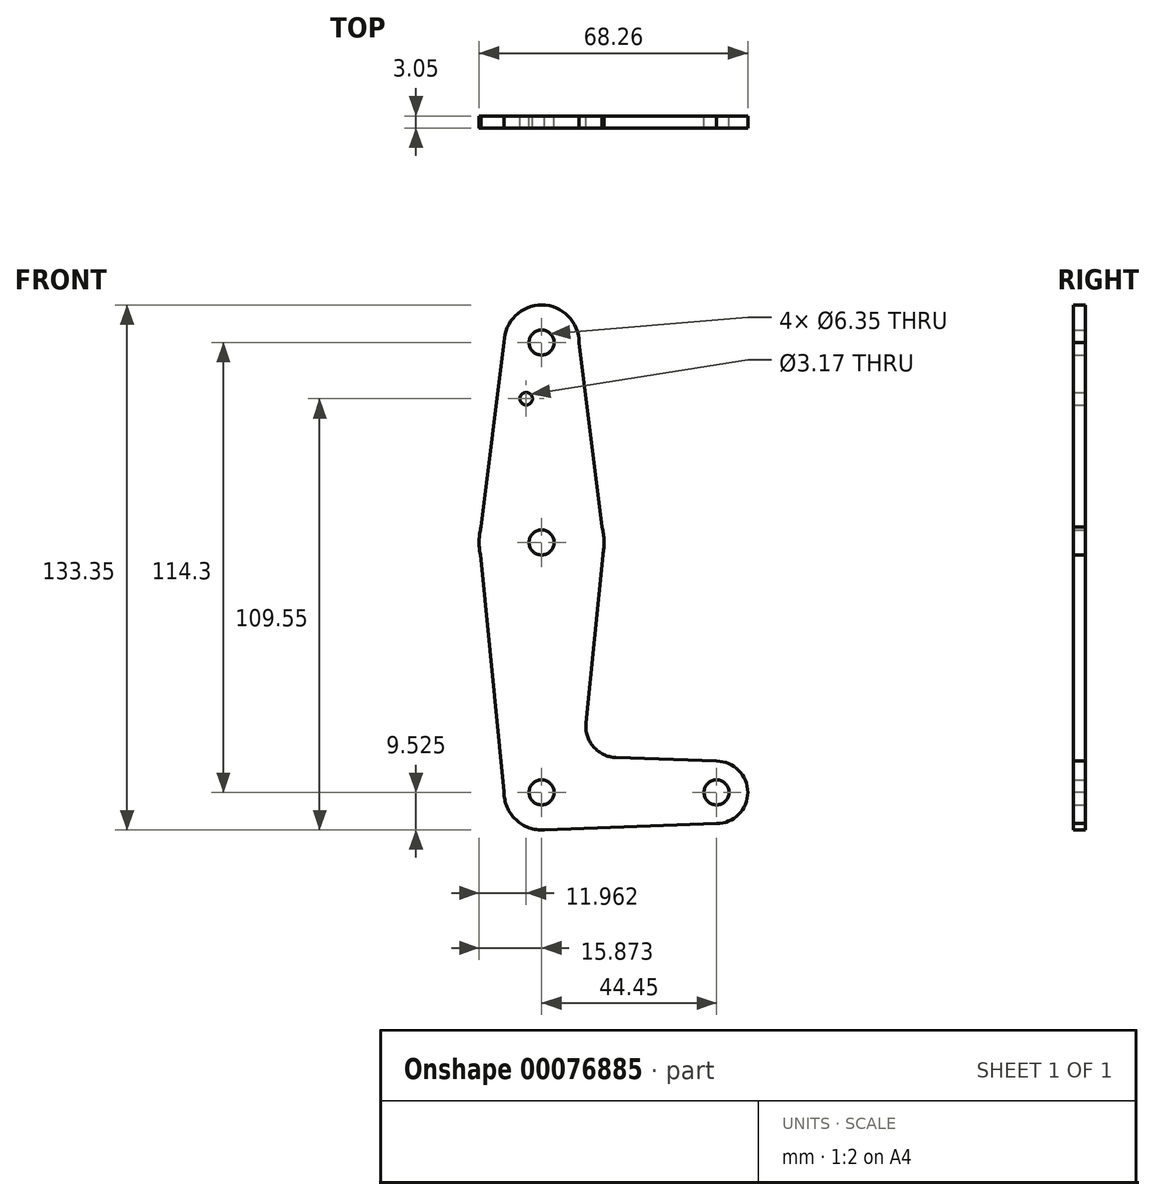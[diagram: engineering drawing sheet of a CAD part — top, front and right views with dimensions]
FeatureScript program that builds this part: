
annotation { "Feature Type Name" : "Feature", "Feature Type Description" : "" }
export const myFeature = defineFeature(function(context is Context, id is Id, definition is map)
    precondition{}
    {
        {
            var Q0;
            Q0=qCreatedBy(makeId("Front.planeOp"),FACE);
            var sketch = newSketch(context, id + "F0", { "sketchPlane" : qUnion([Q0])});
            skLineSegment(sketch, "E0", {"start": v(-624.38, 309.9) * mm, "end": v(-624.38, 195.6) * mm, "construction": true});
            skLineSegment(sketch, "E1", {"start": v(-624.38, 195.6) * mm, "end": v(-579.93, 195.6) * mm, "construction": true});
            skCircle(sketch, "E2", {"center": v(-624.38, 309.9) * mm, "radius": 9.53 * mm});
            skCircle(sketch, "E3", {"center": v(-624.38, 195.6) * mm, "radius": 9.53 * mm});
            skCircle(sketch, "E4", {"center": v(-579.93, 195.6) * mm, "radius": 7.94 * mm});
            skCircle(sketch, "E5", {"center": v(-624.38, 259.1) * mm, "radius": 15.88 * mm});
            skLineSegment(sketch, "E6", {"start": v(-633.9, 310) * mm, "end": v(-640.25, 259.02) * mm});
            skLineSegment(sketch, "E7", {"start": v(-640.25, 259.02) * mm, "end": v(-633.9, 195.71) * mm});
            skLineSegment(sketch, "E8", {"start": v(-614.85, 309.9) * mm, "end": v(-608.5, 259.1) * mm});
            skLineSegment(sketch, "E9", {"start": v(-608.5, 259.1) * mm, "end": v(-613.1, 213.18) * mm});
            skLineSegment(sketch, "E10", {"start": v(-605.47, 204.44) * mm, "end": v(-579.93, 203.53) * mm});
            skLineSegment(sketch, "E11", {"start": v(-624.38, 186.07) * mm, "end": v(-579.93, 187.66) * mm});
            skCircle(sketch, "E12", {"center": v(-624.38, 309.9) * mm, "radius": 3.18 * mm});
            skCircle(sketch, "E13", {"center": v(-624.38, 259.1) * mm, "radius": 3.18 * mm});
            skCircle(sketch, "E14", {"center": v(-628.29, 295.62) * mm, "radius": 1.59 * mm});
            skCircle(sketch, "E15", {"center": v(-624.38, 195.6) * mm, "radius": 3.18 * mm});
            skCircle(sketch, "E16", {"center": v(-579.93, 195.6) * mm, "radius": 3.18 * mm});
            skArc(sketch, "E17.filletArc", {"start": v(-613.1, 213.18) * mm, "mid": v(-611.17, 207.16) * mm, "end": v(-605.47, 204.44) * mm});
            skSolve(sketch);
        }
        {
            var Q0;
            Q0 = qSketchRegion(id + "F0", true);
            extrude(context, id + "F1", {"entities" : qUnion([Q0]), "depth" : 3.05 * mm});
        }
    });
